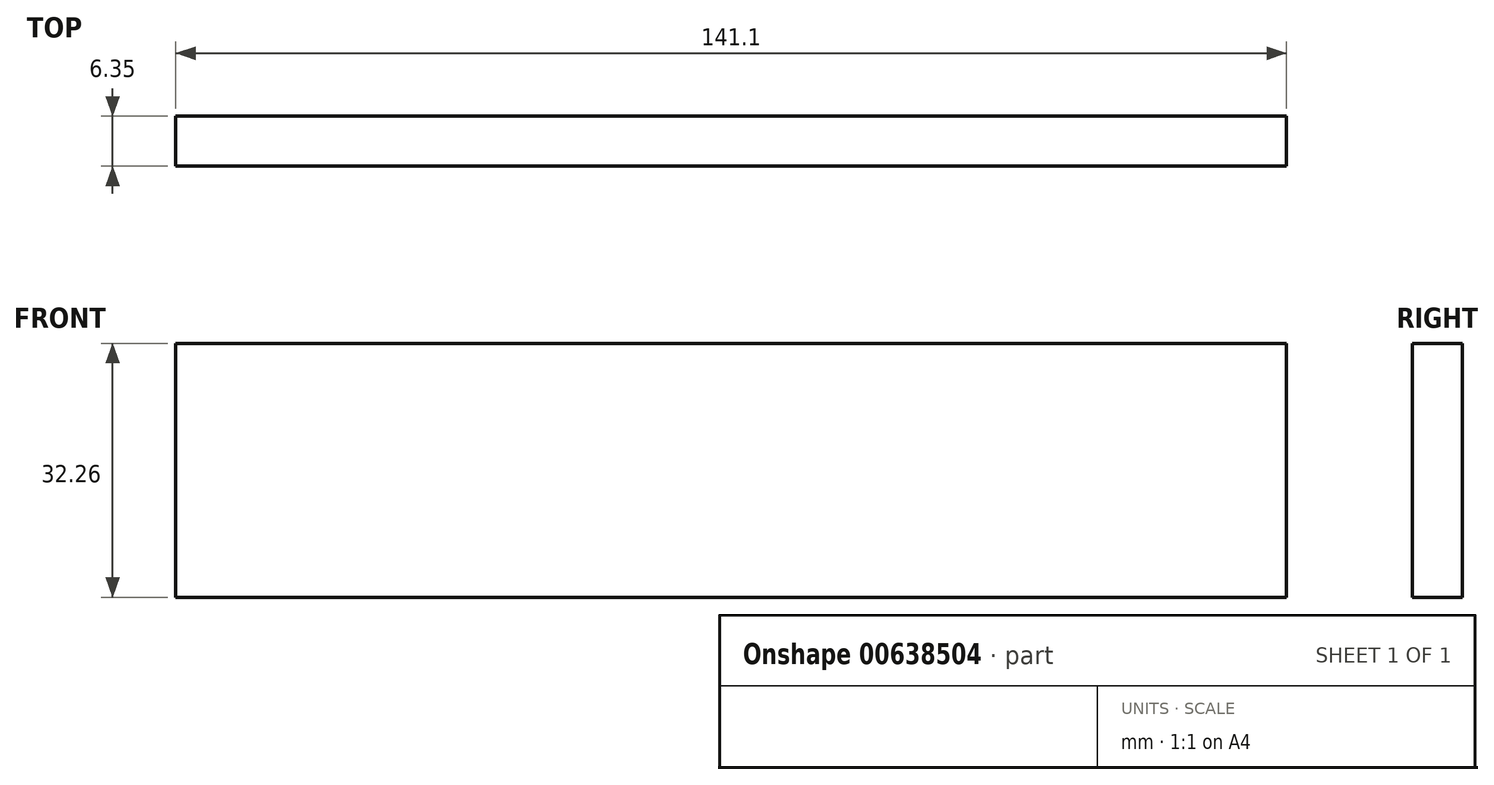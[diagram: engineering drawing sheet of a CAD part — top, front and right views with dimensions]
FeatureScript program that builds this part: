
annotation { "Feature Type Name" : "Feature", "Feature Type Description" : "" }
export const myFeature = defineFeature(function(context is Context, id is Id, definition is map)
    precondition{}
    {
        {
            var Q0;
            Q0=qCreatedBy(makeId("Front.planeOp"),FACE);
            var sketch = newSketch(context, id + "F0", { "sketchPlane" : qUnion([Q0])});
            skLineSegment(sketch, "E0.bottom", {"start": v(-61.03, -39.43) * mm, "end": v(80.07, -39.43) * mm});
            skLineSegment(sketch, "E0.top", {"start": v(-61.03, -71.69) * mm, "end": v(80.07, -71.69) * mm});
            skLineSegment(sketch, "E0.left", {"start": v(-61.03, -39.43) * mm, "end": v(-61.03, -71.69) * mm});
            skLineSegment(sketch, "E0.right", {"start": v(80.07, -39.43) * mm, "end": v(80.07, -71.69) * mm});
            skSolve(sketch);
        }
        {
            var Q0;
            Q0 = qSketchRegion(id + "F0", true);
            extrude(context, id + "F1", {"entities" : qUnion([Q0]), "depth" : 6.35 * mm, "offsetDistance" : 25.4 * mm});
        }
    });
